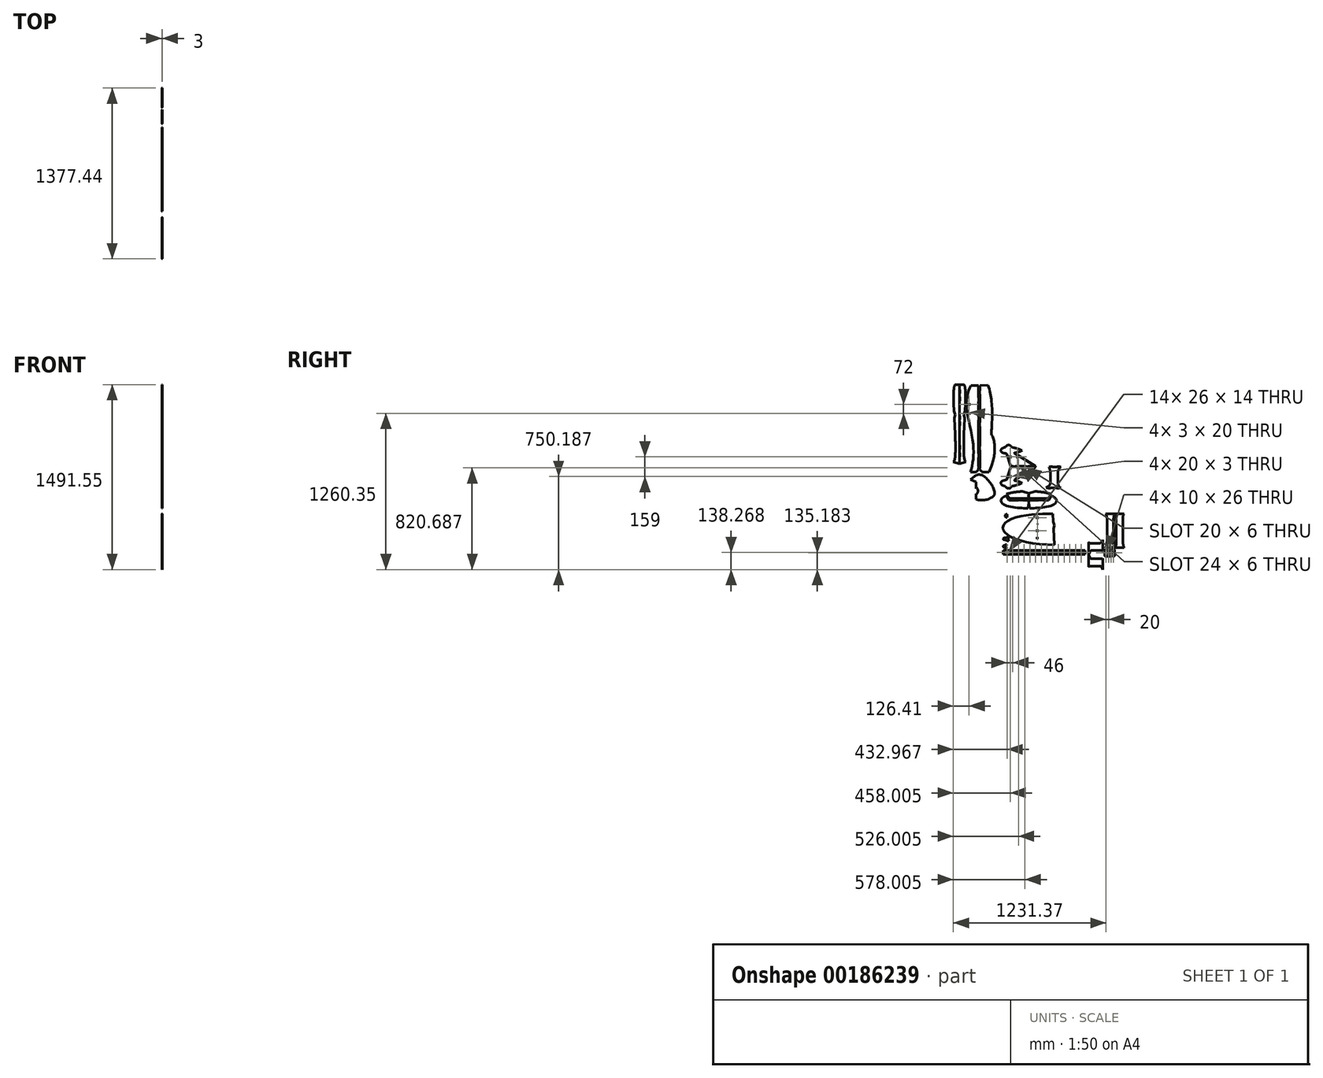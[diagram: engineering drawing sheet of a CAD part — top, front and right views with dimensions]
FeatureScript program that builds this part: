
annotation { "Feature Type Name" : "Feature", "Feature Type Description" : "" }
export const myFeature = defineFeature(function(context is Context, id is Id, definition is map)
    precondition{}
    {
        {
            var Q0;
            Q0=qCreatedBy(makeId("Right.planeOp"),FACE);
            var sketch = newSketch(context, id + "F0", { "sketchPlane" : qUnion([Q0])});
            skLineSegment(sketch, "E0", {"start": v(27.92, -28.88) * mm, "end": v(27.92, -378.88) * mm, "construction": true});
            skLineSegment(sketch, "E1", {"start": v(443.25, -23) * mm, "end": v(445.98, -85.39) * mm});
            skLineSegment(sketch, "E2", {"start": v(485.12, -6.25) * mm, "end": v(485.12, -297.85) * mm, "construction": true});
            skLineSegment(sketch, "E3", {"start": v(455, -114) * mm, "end": v(445.98, -85.39) * mm});
            skLineSegment(sketch, "E4", {"start": v(455, -114) * mm, "end": v(448.5, -143.29) * mm});
            skLineSegment(sketch, "E5.trimOffspring", {"start": v(448.5, -143.29) * mm, "end": v(454.12, -271.76) * mm});
            skFitSpline(sketch, "E6", {"points": [v(443.25, -23) * mm, v(273.48, -28) * mm, v(111.44, -63.42) * mm, v(51, -105.27) * mm, v(39.62, -138.6) * mm, v(65.24, -181.81) * mm, v(180.48, -236.77) * mm, v(454.12, -271.76) * mm], "startDerivative": vector(-965.41, -1.88) * mm, "endDerivative": vector(1440.75, 7.86) * mm});
            skLineSegment(sketch, "E7.bottom", {"start": v(316, -44) * mm, "end": v(319, -44) * mm});
            skLineSegment(sketch, "E7.top", {"start": v(316, -64) * mm, "end": v(319, -64) * mm});
            skLineSegment(sketch, "E7.left", {"start": v(316, -44) * mm, "end": v(316, -64) * mm});
            skLineSegment(sketch, "E7.right", {"start": v(319, -44) * mm, "end": v(319, -64) * mm});
            skLineSegment(sketch, "E8.bottom", {"start": v(316, -148) * mm, "end": v(319, -148) * mm});
            skLineSegment(sketch, "E8.top", {"start": v(316, -168) * mm, "end": v(319, -168) * mm});
            skLineSegment(sketch, "E8.left", {"start": v(316, -148) * mm, "end": v(316, -168) * mm});
            skLineSegment(sketch, "E8.right", {"start": v(319, -148) * mm, "end": v(319, -168) * mm});
            skLineSegment(sketch, "E9.bottom", {"start": v(316, -210) * mm, "end": v(319, -210) * mm});
            skLineSegment(sketch, "E9.top", {"start": v(316, -225) * mm, "end": v(319, -225) * mm});
            skLineSegment(sketch, "E9.left", {"start": v(316, -210) * mm, "end": v(316, -225) * mm});
            skLineSegment(sketch, "E9.right", {"start": v(319, -210) * mm, "end": v(319, -225) * mm});
            skCircle(sketch, "E10", {"center": v(320, -104.5) * mm, "radius": 1 * mm});
            skLineSegment(sketch, "E11", {"start": v(-356.55, 868.4) * mm, "end": v(-353.82, 806.01) * mm});
            skLineSegment(sketch, "E12", {"start": v(-309.8, 1019.4) * mm, "end": v(-309.8, 979.4) * mm});
            skLineSegment(sketch, "E13", {"start": v(-309.8, 380.9) * mm, "end": v(-359.91, 398.16) * mm});
            skLineSegment(sketch, "E14", {"start": v(-344.8, 777.4) * mm, "end": v(-353.82, 806.01) * mm});
            skLineSegment(sketch, "E15", {"start": v(-344.8, 777.4) * mm, "end": v(-351.3, 748.11) * mm});
            skLineSegment(sketch, "E16", {"start": v(-309.8, 1019.4) * mm, "end": v(-345.3, 1019.4) * mm});
            skLineSegment(sketch, "E17.trimOffspring", {"start": v(-351.3, 748.11) * mm, "end": v(-345.68, 619.64) * mm});
            skFitSpline(sketch, "E18", {"points": [v(-356.55, 868.4) * mm, v(-356.83, 968.97) * mm, v(-352.43, 1005.55) * mm, v(-349.11, 1014.93) * mm, v(-346.93, 1018.82) * mm, v(-345.3, 1019.4) * mm], "startDerivative": vector(-12.13, 345.27) * mm, "endDerivative": vector(43.94, 0.31) * mm});
            skFitSpline(sketch, "E19", {"points": [v(-345.68, 619.64) * mm, v(-342.97, 524.45) * mm, v(-346.35, 432.06) * mm, v(-353.3, 404.18) * mm, v(-359.91, 398.16) * mm], "startDerivative": vector(19, -544.1) * mm, "endDerivative": vector(-110.93, -29.86) * mm});
            skLineSegment(sketch, "E20", {"start": v(-309.8, 979.4) * mm, "end": v(-311.3, 979.4) * mm});
            skLineSegment(sketch, "E21", {"start": v(-311.3, 979.4) * mm, "end": v(-311.3, 949.4) * mm});
            skLineSegment(sketch, "E22", {"start": v(-311.3, 949.4) * mm, "end": v(-309.8, 949.4) * mm});
            skLineSegment(sketch, "E23", {"start": v(-309.8, 919.4) * mm, "end": v(-311.3, 919.4) * mm});
            skLineSegment(sketch, "E24", {"start": v(-311.3, 919.4) * mm, "end": v(-311.3, 889.4) * mm});
            skLineSegment(sketch, "E25", {"start": v(-311.3, 889.4) * mm, "end": v(-309.8, 889.4) * mm});
            skLineSegment(sketch, "E26", {"start": v(-309.8, 769.4) * mm, "end": v(-311.3, 769.4) * mm});
            skLineSegment(sketch, "E27", {"start": v(-311.3, 769.4) * mm, "end": v(-311.3, 739.4) * mm});
            skLineSegment(sketch, "E28", {"start": v(-311.3, 739.4) * mm, "end": v(-309.8, 739.4) * mm});
            skLineSegment(sketch, "E29", {"start": v(-309.8, 719.4) * mm, "end": v(-311.3, 719.4) * mm});
            skLineSegment(sketch, "E30", {"start": v(-311.3, 719.4) * mm, "end": v(-311.3, 689.4) * mm});
            skLineSegment(sketch, "E31", {"start": v(-311.3, 689.4) * mm, "end": v(-309.8, 689.4) * mm});
            skLineSegment(sketch, "E32", {"start": v(-309.8, 529.4) * mm, "end": v(-311.3, 529.4) * mm});
            skLineSegment(sketch, "E33", {"start": v(-311.3, 529.4) * mm, "end": v(-311.3, 499.4) * mm});
            skLineSegment(sketch, "E34", {"start": v(-311.3, 499.4) * mm, "end": v(-309.8, 499.4) * mm});
            skLineSegment(sketch, "E35", {"start": v(-309.8, 469.4) * mm, "end": v(-311.3, 469.4) * mm});
            skLineSegment(sketch, "E36", {"start": v(-311.3, 469.4) * mm, "end": v(-311.3, 439.4) * mm});
            skLineSegment(sketch, "E37", {"start": v(-311.3, 439.4) * mm, "end": v(-309.8, 439.4) * mm});
            skLineSegment(sketch, "E38.trimOffspring", {"start": v(-309.8, 949.4) * mm, "end": v(-309.8, 919.4) * mm});
            skLineSegment(sketch, "E39.trimOffspring", {"start": v(-309.8, 889.4) * mm, "end": v(-309.8, 769.4) * mm});
            skLineSegment(sketch, "E40.trimOffspring", {"start": v(-309.8, 739.4) * mm, "end": v(-309.8, 719.4) * mm});
            skLineSegment(sketch, "E41.trimOffspring", {"start": v(-309.8, 689.4) * mm, "end": v(-309.8, 529.4) * mm});
            skLineSegment(sketch, "E42.trimOffspring", {"start": v(-309.8, 499.4) * mm, "end": v(-309.8, 469.4) * mm});
            skLineSegment(sketch, "E43.trimOffspring", {"start": v(-309.8, 439.4) * mm, "end": v(-309.8, 380.9) * mm});
            skLineSegment(sketch, "E44", {"start": v(-144.2, 1013.2) * mm, "end": v(-144.2, 973.2) * mm});
            skLineSegment(sketch, "E45", {"start": v(-144.2, 334.7) * mm, "end": v(-124.7, 314.56) * mm});
            skLineSegment(sketch, "E46", {"start": v(-124.7, 314.56) * mm, "end": v(-72.7, 314.56) * mm});
            skLineSegment(sketch, "E47", {"start": v(-144.2, 973.2) * mm, "end": v(-147.2, 973.2) * mm});
            skLineSegment(sketch, "E48", {"start": v(-147.2, 973.2) * mm, "end": v(-147.2, 943.2) * mm});
            skLineSegment(sketch, "E49", {"start": v(-147.2, 943.2) * mm, "end": v(-144.2, 943.2) * mm});
            skLineSegment(sketch, "E50", {"start": v(-144.2, 713.2) * mm, "end": v(-147.2, 713.2) * mm});
            skLineSegment(sketch, "E51", {"start": v(-147.2, 713.2) * mm, "end": v(-147.2, 683.2) * mm});
            skLineSegment(sketch, "E52", {"start": v(-147.2, 683.2) * mm, "end": v(-144.2, 683.2) * mm});
            skLineSegment(sketch, "E53", {"start": v(-144.2, 523.2) * mm, "end": v(-147.2, 523.2) * mm});
            skLineSegment(sketch, "E54", {"start": v(-147.2, 523.2) * mm, "end": v(-147.2, 493.2) * mm});
            skLineSegment(sketch, "E55", {"start": v(-147.2, 493.2) * mm, "end": v(-144.2, 493.2) * mm});
            skLineSegment(sketch, "E56", {"start": v(-144.2, 344.7) * mm, "end": v(-147.2, 344.7) * mm});
            skLineSegment(sketch, "E57", {"start": v(-147.2, 344.7) * mm, "end": v(-147.2, 334.7) * mm});
            skLineSegment(sketch, "E58", {"start": v(-147.2, 334.7) * mm, "end": v(-144.2, 334.7) * mm});
            skLineSegment(sketch, "E59.trimOffspring", {"start": v(-144.2, 493.2) * mm, "end": v(-144.2, 344.7) * mm});
            skLineSegment(sketch, "E60.trimOffspring", {"start": v(-144.2, 683.2) * mm, "end": v(-144.2, 523.2) * mm});
            skLineSegment(sketch, "E61.trimOffspring", {"start": v(-144.2, 943.2) * mm, "end": v(-144.2, 713.2) * mm});
            skLineSegment(sketch, "E62", {"start": v(-144.2, 1013.2) * mm, "end": v(-82.22, 1014.82) * mm});
            skFitSpline(sketch, "E63", {"points": [v(-82.22, 1014.82) * mm, v(-52.5, 891.86) * mm, v(-47.86, 740.86) * mm, v(-54.44, 620.7) * mm], "startDerivative": vector(163.45, -369.94) * mm, "endDerivative": vector(-24, -362.98) * mm});
            skLineSegment(sketch, "E64", {"start": v(-157, 1013.2) * mm, "end": v(-157, 913.2) * mm});
            skLineSegment(sketch, "E65", {"start": v(-157, 334.7) * mm, "end": v(-177, 314.56) * mm});
            skLineSegment(sketch, "E66", {"start": v(-177, 314.56) * mm, "end": v(-222, 314.56) * mm});
            skLineSegment(sketch, "E67", {"start": v(-157, 1013.2) * mm, "end": v(-218.98, 1011.58) * mm});
            skLineSegment(sketch, "E68", {"start": v(-157, 913.2) * mm, "end": v(-154, 913.2) * mm});
            skLineSegment(sketch, "E69", {"start": v(-154, 913.2) * mm, "end": v(-154, 883.2) * mm});
            skLineSegment(sketch, "E70", {"start": v(-154, 883.2) * mm, "end": v(-157, 883.2) * mm});
            skLineSegment(sketch, "E71", {"start": v(-157, 763.2) * mm, "end": v(-154, 763.2) * mm});
            skLineSegment(sketch, "E72", {"start": v(-154, 763.2) * mm, "end": v(-154, 733.2) * mm});
            skLineSegment(sketch, "E73", {"start": v(-154, 733.2) * mm, "end": v(-157, 733.2) * mm});
            skLineSegment(sketch, "E74", {"start": v(-157, 463.2) * mm, "end": v(-154, 463.2) * mm});
            skLineSegment(sketch, "E75", {"start": v(-154, 463.2) * mm, "end": v(-154, 433.2) * mm});
            skLineSegment(sketch, "E76", {"start": v(-154, 433.2) * mm, "end": v(-157, 433.2) * mm});
            skLineSegment(sketch, "E77", {"start": v(-157, 359.7) * mm, "end": v(-154, 359.7) * mm});
            skLineSegment(sketch, "E78", {"start": v(-154, 359.7) * mm, "end": v(-154, 349.7) * mm});
            skLineSegment(sketch, "E79", {"start": v(-154, 349.7) * mm, "end": v(-157, 349.7) * mm});
            skLineSegment(sketch, "E80.trimOffspring", {"start": v(-157, 349.7) * mm, "end": v(-157, 334.7) * mm});
            skLineSegment(sketch, "E81.trimOffspring", {"start": v(-157, 433.2) * mm, "end": v(-157, 359.7) * mm});
            skLineSegment(sketch, "E82.trimOffspring", {"start": v(-157, 733.2) * mm, "end": v(-157, 463.2) * mm});
            skLineSegment(sketch, "E83.trimOffspring", {"start": v(-157, 883.2) * mm, "end": v(-157, 763.2) * mm});
            skFitSpline(sketch, "E84", {"points": [v(-222, 314.56) * mm, v(-200.27, 420.75) * mm, v(-204.03, 569.28) * mm, v(-247.79, 793.5) * mm, v(-249.4, 929.59) * mm, v(-218.98, 1011.58) * mm], "startDerivative": vector(155.72, 450.4) * mm, "endDerivative": vector(203.74, 370.62) * mm});
            skLineSegment(sketch, "E85", {"start": v(-176.43, 234.38) * mm, "end": v(-176.43, 182.38) * mm});
            skLineSegment(sketch, "E86", {"start": v(-176.43, 139.88) * mm, "end": v(-176.43, 94.88) * mm});
            skArc(sketch, "E87", {"start": v(-119.34, 284.4) * mm, "mid": v(-152.52, 294.07) * mm, "end": v(-185.06, 282.42) * mm});
            skArc(sketch, "E88", {"start": v(-40.5, 117.7) * mm, "mid": v(-28.29, 134.7) * mm, "end": v(-27.63, 155.64) * mm});
            skArc(sketch, "E89", {"start": v(-176.43, 94.88) * mm, "mid": v(-105.63, 89.44) * mm, "end": v(-40.5, 117.7) * mm});
            skArc(sketch, "E90", {"start": v(-27.63, 155.64) * mm, "mid": v(-61.96, 228.23) * mm, "end": v(-119.34, 284.4) * mm});
            skLineSegment(sketch, "E91", {"start": v(-222.68, 253.38) * mm, "end": v(-185.06, 282.42) * mm});
            skPoint(sketch, "E92", {"position": v(-53.7, 360.81) * mm});
            skLineSegment(sketch, "E93", {"start": v(-72.7, 314.56) * mm, "end": v(-53.7, 360.81) * mm});
            skFitSpline(sketch, "E94", {"points": [v(-53.7, 360.81) * mm, v(-30.19, 450.47) * mm, v(-30.24, 553.44) * mm, v(-54.44, 620.7) * mm], "startDerivative": vector(84.05, 239.81) * mm, "endDerivative": vector(-123.94, 199.65) * mm});
            skLineSegment(sketch, "E95", {"start": v(-176.43, 234.38) * mm, "end": v(-222.68, 253.38) * mm});
            skLineSegment(sketch, "E96", {"start": v(248.03, 141.56) * mm, "end": v(248.03, 126.56) * mm});
            skLineSegment(sketch, "E97", {"start": v(248.03, 111.56) * mm, "end": v(246.53, 111.56) * mm});
            skLineSegment(sketch, "E98", {"start": v(246.53, 111.56) * mm, "end": v(246.53, 101.56) * mm});
            skLineSegment(sketch, "E99", {"start": v(246.53, 101.56) * mm, "end": v(88.53, 101.56) * mm});
            skLineSegment(sketch, "E100", {"start": v(88.53, 101.56) * mm, "end": v(68.03, 137.06) * mm});
            skLineSegment(sketch, "E101", {"start": v(248.03, 141.56) * mm, "end": v(197.92, 158.81) * mm});
            skLineSegment(sketch, "E102", {"start": v(248.03, 116.56) * mm, "end": v(246.53, 116.56) * mm});
            skLineSegment(sketch, "E103", {"start": v(246.53, 116.56) * mm, "end": v(246.53, 126.56) * mm});
            skLineSegment(sketch, "E104", {"start": v(246.53, 126.56) * mm, "end": v(248.03, 126.56) * mm});
            skLineSegment(sketch, "E105.trimOffspring", {"start": v(248.03, 116.56) * mm, "end": v(248.03, 111.56) * mm});
            skFitSpline(sketch, "E106", {"points": [v(68.03, 137.06) * mm, v(127.3, 151) * mm, v(197.92, 158.81) * mm], "startDerivative": vector(116.05, 38.24) * mm, "endDerivative": vector(126.97, 8.86) * mm});
            skLineSegment(sketch, "E107", {"start": v(68.03, 122.99) * mm, "end": v(88.53, 87.48) * mm});
            skLineSegment(sketch, "E108", {"start": v(88.53, 87.48) * mm, "end": v(248.03, 87.48) * mm});
            skLineSegment(sketch, "E109", {"start": v(248.03, 87.48) * mm, "end": v(248.03, 55.48) * mm});
            skLineSegment(sketch, "E110", {"start": v(248.03, 55.48) * mm, "end": v(244.03, 55.48) * mm});
            skLineSegment(sketch, "E111", {"start": v(244.03, 55.48) * mm, "end": v(241.73, 22.56) * mm});
            skFitSpline(sketch, "E112", {"points": [v(68.03, 122.99) * mm, v(36.37, 107.72) * mm, v(23.55, 87.23) * mm, v(38.07, 58.37) * mm, v(125.76, 29.82) * mm, v(241.73, 22.56) * mm], "startDerivative": vector(-166.1, -58.4) * mm, "endDerivative": vector(399.12, -7.54) * mm});
            skLineSegment(sketch, "E113", {"start": v(101.1, 354.54) * mm, "end": v(120.1, 354.54) * mm});
            skLineSegment(sketch, "E114", {"start": v(120.1, 354.54) * mm, "end": v(120.1, 357.54) * mm});
            skLineSegment(sketch, "E115", {"start": v(120.1, 357.54) * mm, "end": v(140.1, 357.54) * mm});
            skLineSegment(sketch, "E116", {"start": v(140.1, 357.54) * mm, "end": v(140.1, 354.54) * mm});
            skLineSegment(sketch, "E117", {"start": v(140.1, 354.54) * mm, "end": v(224.1, 354.54) * mm});
            skLineSegment(sketch, "E118", {"start": v(224.1, 354.54) * mm, "end": v(224.1, 357.54) * mm});
            skLineSegment(sketch, "E119", {"start": v(224.1, 357.54) * mm, "end": v(244.1, 357.54) * mm});
            skLineSegment(sketch, "E120", {"start": v(244.1, 357.54) * mm, "end": v(244.1, 354.54) * mm});
            skLineSegment(sketch, "E121", {"start": v(244.1, 354.54) * mm, "end": v(286.1, 354.54) * mm});
            skLineSegment(sketch, "E122", {"start": v(286.1, 354.54) * mm, "end": v(286.1, 357.54) * mm});
            skLineSegment(sketch, "E123", {"start": v(286.1, 357.54) * mm, "end": v(301.1, 357.54) * mm});
            skLineSegment(sketch, "E124", {"start": v(301.1, 357.54) * mm, "end": v(301.1, 354.54) * mm});
            skLineSegment(sketch, "E125", {"start": v(301.1, 354.54) * mm, "end": v(128.72, 246.8) * mm});
            skLineSegment(sketch, "E126", {"start": v(101.1, 354.54) * mm, "end": v(69.08, 251.02) * mm});
            skFitSpline(sketch, "E127", {"points": [v(69.08, 251.02) * mm, v(30.4, 239.54) * mm, v(23.23, 226.4) * mm, v(31.82, 210.74) * mm, v(60.87, 200.12) * mm], "startDerivative": vector(-185.57, -20.9) * mm, "endDerivative": vector(122.55, -13.98) * mm});
            skFitSpline(sketch, "E128", {"points": [v(128.72, 246.8) * mm, v(164.15, 239.14) * mm, v(193.63, 226.66) * mm], "startDerivative": vector(69.66, -10.84) * mm, "endDerivative": vector(67.95, -41.44) * mm});
            skFitSpline(sketch, "E129", {"points": [v(193.63, 226.66) * mm, v(152.17, 210.06) * mm, v(110.29, 200.98) * mm], "startDerivative": vector(-63.37, -40.2) * mm, "endDerivative": vector(-87.44, -10.73) * mm});
            skArc(sketch, "E130", {"start": v(60.87, 200.12) * mm, "mid": v(85.89, 182.63) * mm, "end": v(110.29, 200.98) * mm});
            skLineSegment(sketch, "E131.bottom", {"start": v(-235, 870.2) * mm, "end": v(-232, 870.2) * mm});
            skLineSegment(sketch, "E131.top", {"start": v(-235, 850.2) * mm, "end": v(-232, 850.2) * mm});
            skLineSegment(sketch, "E131.left", {"start": v(-235, 870.2) * mm, "end": v(-235, 850.2) * mm});
            skLineSegment(sketch, "E131.right", {"start": v(-232, 870.2) * mm, "end": v(-232, 850.2) * mm});
            skLineSegment(sketch, "E132.bottom", {"start": v(-235, 798.2) * mm, "end": v(-232, 798.2) * mm});
            skLineSegment(sketch, "E132.top", {"start": v(-235, 778.2) * mm, "end": v(-232, 778.2) * mm});
            skLineSegment(sketch, "E132.left", {"start": v(-235, 798.2) * mm, "end": v(-235, 778.2) * mm});
            skLineSegment(sketch, "E132.right", {"start": v(-232, 798.2) * mm, "end": v(-232, 778.2) * mm});
            skLineSegment(sketch, "E133.bottom", {"start": v(88.1, 279.54) * mm, "end": v(108.1, 279.54) * mm});
            skLineSegment(sketch, "E133.top", {"start": v(88.1, 276.54) * mm, "end": v(108.1, 276.54) * mm});
            skLineSegment(sketch, "E133.left", {"start": v(88.1, 279.54) * mm, "end": v(88.1, 276.54) * mm});
            skLineSegment(sketch, "E133.right", {"start": v(108.1, 279.54) * mm, "end": v(108.1, 276.54) * mm});
            skLineSegment(sketch, "E134.bottom", {"start": v(146.1, 279.54) * mm, "end": v(166.1, 279.54) * mm});
            skLineSegment(sketch, "E134.top", {"start": v(146.1, 276.54) * mm, "end": v(166.1, 276.54) * mm});
            skLineSegment(sketch, "E134.left", {"start": v(146.1, 279.54) * mm, "end": v(146.1, 276.54) * mm});
            skLineSegment(sketch, "E134.right", {"start": v(166.1, 279.54) * mm, "end": v(166.1, 276.54) * mm});
            skLineSegment(sketch, "E135", {"start": v(409, 355.87) * mm, "end": v(420, 355.87) * mm});
            skLineSegment(sketch, "E136", {"start": v(420, 355.87) * mm, "end": v(420, 358.87) * mm});
            skLineSegment(sketch, "E137", {"start": v(420, 358.87) * mm, "end": v(440, 358.87) * mm});
            skLineSegment(sketch, "E138", {"start": v(440, 358.87) * mm, "end": v(440, 355.87) * mm});
            skLineSegment(sketch, "E139", {"start": v(440, 355.87) * mm, "end": v(478, 355.87) * mm});
            skLineSegment(sketch, "E140", {"start": v(478, 355.87) * mm, "end": v(478, 358.87) * mm});
            skLineSegment(sketch, "E141", {"start": v(478, 358.87) * mm, "end": v(498, 358.87) * mm});
            skLineSegment(sketch, "E142", {"start": v(498, 358.87) * mm, "end": v(498, 355.87) * mm});
            skLineSegment(sketch, "E143", {"start": v(498, 355.87) * mm, "end": v(508, 355.87) * mm});
            skLineSegment(sketch, "E144", {"start": v(409, 355.87) * mm, "end": v(415.72, 341.95) * mm});
            skLineSegment(sketch, "E145", {"start": v(423.45, 308.09) * mm, "end": v(423.45, 233.94) * mm});
            skLineSegment(sketch, "E146", {"start": v(388, 186.37) * mm, "end": v(404.2, 197.45) * mm});
            skLineSegment(sketch, "E147", {"start": v(388, 186.37) * mm, "end": v(403, 186.37) * mm});
            skLineSegment(sketch, "E148", {"start": v(403, 186.37) * mm, "end": v(403, 184.87) * mm});
            skLineSegment(sketch, "E149", {"start": v(403, 184.87) * mm, "end": v(423, 184.87) * mm});
            skLineSegment(sketch, "E150", {"start": v(423, 184.87) * mm, "end": v(423, 186.37) * mm});
            skLineSegment(sketch, "E151", {"start": v(423, 186.37) * mm, "end": v(475, 186.37) * mm});
            skLineSegment(sketch, "E152", {"start": v(475, 186.37) * mm, "end": v(475, 184.87) * mm});
            skLineSegment(sketch, "E153", {"start": v(475, 184.87) * mm, "end": v(495, 184.87) * mm});
            skLineSegment(sketch, "E154", {"start": v(495, 184.87) * mm, "end": v(495, 186.37) * mm});
            skLineSegment(sketch, "E155", {"start": v(495, 186.37) * mm, "end": v(507, 186.37) * mm});
            skLineSegment(sketch, "E156", {"start": v(484.82, 221.62) * mm, "end": v(484.82, 318.58) * mm});
            skArc(sketch, "E157", {"start": v(508, 355.87) * mm, "mid": v(491.09, 340.54) * mm, "end": v(484.82, 318.58) * mm});
            skArc(sketch, "E158", {"start": v(484.82, 221.62) * mm, "mid": v(490.83, 200.8) * mm, "end": v(507, 186.37) * mm});
            skArc(sketch, "E159", {"start": v(423.45, 308.09) * mm, "mid": v(421.5, 325.45) * mm, "end": v(415.72, 341.95) * mm});
            skArc(sketch, "E160", {"start": v(404.2, 197.45) * mm, "mid": v(418.35, 213.31) * mm, "end": v(423.45, 233.94) * mm});
            skLineSegment(sketch, "E161", {"start": v(729.86, -351.15) * mm, "end": v(729.86, -252.15) * mm});
            skLineSegment(sketch, "E162", {"start": v(745.23, -259.1) * mm, "end": v(820.62, -259.1) * mm});
            skLineSegment(sketch, "E163", {"start": v(844.86, -230.15) * mm, "end": v(844.86, -320.15) * mm});
            skLineSegment(sketch, "E164", {"start": v(759.7, -316.87) * mm, "end": v(832.36, -316.87) * mm});
            skLineSegment(sketch, "E165", {"start": v(729.86, -351.15) * mm, "end": v(739.35, -330.04) * mm});
            skLineSegment(sketch, "E166", {"start": v(844.86, -230.15) * mm, "end": v(835.95, -249.32) * mm});
            skArc(sketch, "E167", {"start": v(759.7, -316.87) * mm, "mid": v(747.58, -320.45) * mm, "end": v(739.35, -330.04) * mm});
            skArc(sketch, "E168", {"start": v(844.86, -320.15) * mm, "mid": v(838.82, -317.7) * mm, "end": v(832.36, -316.87) * mm});
            skArc(sketch, "E169", {"start": v(729.86, -252.15) * mm, "mid": v(736.8, -257.29) * mm, "end": v(745.23, -259.1) * mm});
            skArc(sketch, "E170", {"start": v(820.62, -259.1) * mm, "mid": v(829.72, -256.45) * mm, "end": v(835.95, -249.32) * mm});
            skLineSegment(sketch, "E171", {"start": v(867.53, -21.62) * mm, "end": v(942.53, -21.62) * mm});
            skLineSegment(sketch, "E172", {"start": v(878.96, -57.62) * mm, "end": v(878.96, -235.17) * mm});
            skLineSegment(sketch, "E173", {"start": v(867.53, -296.62) * mm, "end": v(942.53, -296.62) * mm});
            skLineSegment(sketch, "E174", {"start": v(932.35, -266.1) * mm, "end": v(932.35, -61.06) * mm});
            skArc(sketch, "E175", {"start": v(878.96, -57.62) * mm, "mid": v(876.04, -38.74) * mm, "end": v(867.53, -21.62) * mm});
            skArc(sketch, "E176", {"start": v(867.53, -296.62) * mm, "mid": v(876.08, -266.42) * mm, "end": v(878.96, -235.17) * mm});
            skArc(sketch, "E177", {"start": v(942.53, -21.62) * mm, "mid": v(934.94, -40.7) * mm, "end": v(932.35, -61.06) * mm});
            skArc(sketch, "E178", {"start": v(932.35, -266.1) * mm, "mid": v(934.97, -282.19) * mm, "end": v(942.53, -296.62) * mm});
            skLineSegment(sketch, "E179.bottom", {"start": v(42.06, -317.88) * mm, "end": v(702.06, -317.88) * mm});
            skLineSegment(sketch, "E179.top", {"start": v(42.06, -349.88) * mm, "end": v(702.06, -349.88) * mm});
            skLineSegment(sketch, "E179.left", {"start": v(42.06, -317.88) * mm, "end": v(42.06, -349.88) * mm});
            skLineSegment(sketch, "E179.right", {"start": v(702.06, -317.88) * mm, "end": v(702.06, -349.88) * mm});
            skLineSegment(sketch, "E180", {"start": v(60.06, -333.88) * mm, "end": v(73.06, -326.88) * mm});
            skLineSegment(sketch, "E181", {"start": v(73.06, -326.88) * mm, "end": v(86.06, -333.88) * mm});
            skLineSegment(sketch, "E182", {"start": v(86.06, -333.88) * mm, "end": v(60.06, -333.88) * mm, "construction": true});
            skLineSegment(sketch, "E183", {"start": v(73.06, -333.88) * mm, "end": v(73.06, -326.88) * mm, "construction": true});
            skLineSegment(sketch, "E184.MirrorCS", {"start": v(60.06, -333.88) * mm, "end": v(73.06, -340.88) * mm});
            skLineSegment(sketch, "E185.MirrorCS", {"start": v(73.06, -340.88) * mm, "end": v(86.06, -333.88) * mm});
            skLineSegment(sketch, "E186.1.0.0", {"start": v(119.06, -326.88) * mm, "end": v(132.06, -333.88) * mm});
            skLineSegment(sketch, "E186.1.0.1", {"start": v(106.06, -333.88) * mm, "end": v(119.06, -326.88) * mm});
            skLineSegment(sketch, "E186.1.0.2", {"start": v(106.06, -333.88) * mm, "end": v(119.06, -340.88) * mm});
            skLineSegment(sketch, "E186.1.0.3", {"start": v(119.06, -340.88) * mm, "end": v(132.06, -333.88) * mm});
            skLineSegment(sketch, "E186.2.0.0", {"start": v(165.06, -326.88) * mm, "end": v(178.06, -333.88) * mm});
            skLineSegment(sketch, "E186.2.0.1", {"start": v(152.06, -333.88) * mm, "end": v(165.06, -326.88) * mm});
            skLineSegment(sketch, "E186.2.0.2", {"start": v(152.06, -333.88) * mm, "end": v(165.06, -340.88) * mm});
            skLineSegment(sketch, "E186.2.0.3", {"start": v(165.06, -340.88) * mm, "end": v(178.06, -333.88) * mm});
            skLineSegment(sketch, "E186.direction1", {"start": v(73.06, -326.88) * mm, "end": v(119.06, -326.88) * mm, "construction": true});
            skLineSegment(sketch, "E187.0.3.0", {"start": v(211.06, -326.88) * mm, "end": v(224.06, -333.88) * mm});
            skLineSegment(sketch, "E187.3.3.0", {"start": v(198.06, -333.88) * mm, "end": v(211.06, -326.88) * mm});
            skLineSegment(sketch, "E187.6.3.0", {"start": v(198.06, -333.88) * mm, "end": v(211.06, -340.88) * mm});
            skLineSegment(sketch, "E187.9.3.0", {"start": v(211.06, -340.88) * mm, "end": v(224.06, -333.88) * mm});
            skLineSegment(sketch, "E187.0.4.0", {"start": v(257.06, -326.88) * mm, "end": v(270.06, -333.88) * mm});
            skLineSegment(sketch, "E187.3.4.0", {"start": v(244.06, -333.88) * mm, "end": v(257.06, -326.88) * mm});
            skLineSegment(sketch, "E187.6.4.0", {"start": v(244.06, -333.88) * mm, "end": v(257.06, -340.88) * mm});
            skLineSegment(sketch, "E187.9.4.0", {"start": v(257.06, -340.88) * mm, "end": v(270.06, -333.88) * mm});
            skLineSegment(sketch, "E187.0.5.0", {"start": v(303.06, -326.88) * mm, "end": v(316.06, -333.88) * mm});
            skLineSegment(sketch, "E187.3.5.0", {"start": v(290.06, -333.88) * mm, "end": v(303.06, -326.88) * mm});
            skLineSegment(sketch, "E187.6.5.0", {"start": v(290.06, -333.88) * mm, "end": v(303.06, -340.88) * mm});
            skLineSegment(sketch, "E187.9.5.0", {"start": v(303.06, -340.88) * mm, "end": v(316.06, -333.88) * mm});
            skLineSegment(sketch, "E187.0.6.0", {"start": v(349.06, -326.88) * mm, "end": v(362.06, -333.88) * mm});
            skLineSegment(sketch, "E187.3.6.0", {"start": v(336.06, -333.88) * mm, "end": v(349.06, -326.88) * mm});
            skLineSegment(sketch, "E187.6.6.0", {"start": v(336.06, -333.88) * mm, "end": v(349.06, -340.88) * mm});
            skLineSegment(sketch, "E187.9.6.0", {"start": v(349.06, -340.88) * mm, "end": v(362.06, -333.88) * mm});
            skLineSegment(sketch, "E187.0.7.0", {"start": v(395.06, -326.88) * mm, "end": v(408.06, -333.88) * mm});
            skLineSegment(sketch, "E187.3.7.0", {"start": v(382.06, -333.88) * mm, "end": v(395.06, -326.88) * mm});
            skLineSegment(sketch, "E187.6.7.0", {"start": v(382.06, -333.88) * mm, "end": v(395.06, -340.88) * mm});
            skLineSegment(sketch, "E187.9.7.0", {"start": v(395.06, -340.88) * mm, "end": v(408.06, -333.88) * mm});
            skLineSegment(sketch, "E187.0.8.0", {"start": v(441.06, -326.88) * mm, "end": v(454.06, -333.88) * mm});
            skLineSegment(sketch, "E187.3.8.0", {"start": v(428.06, -333.88) * mm, "end": v(441.06, -326.88) * mm});
            skLineSegment(sketch, "E187.6.8.0", {"start": v(428.06, -333.88) * mm, "end": v(441.06, -340.88) * mm});
            skLineSegment(sketch, "E187.9.8.0", {"start": v(441.06, -340.88) * mm, "end": v(454.06, -333.88) * mm});
            skLineSegment(sketch, "E187.0.9.0", {"start": v(487.06, -326.88) * mm, "end": v(500.06, -333.88) * mm});
            skLineSegment(sketch, "E187.3.9.0", {"start": v(474.06, -333.88) * mm, "end": v(487.06, -326.88) * mm});
            skLineSegment(sketch, "E187.6.9.0", {"start": v(474.06, -333.88) * mm, "end": v(487.06, -340.88) * mm});
            skLineSegment(sketch, "E187.9.9.0", {"start": v(487.06, -340.88) * mm, "end": v(500.06, -333.88) * mm});
            skLineSegment(sketch, "E187.0.10.0", {"start": v(533.06, -326.88) * mm, "end": v(546.06, -333.88) * mm});
            skLineSegment(sketch, "E187.3.10.0", {"start": v(520.06, -333.88) * mm, "end": v(533.06, -326.88) * mm});
            skLineSegment(sketch, "E187.6.10.0", {"start": v(520.06, -333.88) * mm, "end": v(533.06, -340.88) * mm});
            skLineSegment(sketch, "E187.9.10.0", {"start": v(533.06, -340.88) * mm, "end": v(546.06, -333.88) * mm});
            skLineSegment(sketch, "E187.0.11.0", {"start": v(579.06, -326.88) * mm, "end": v(592.06, -333.88) * mm});
            skLineSegment(sketch, "E187.3.11.0", {"start": v(566.06, -333.88) * mm, "end": v(579.06, -326.88) * mm});
            skLineSegment(sketch, "E187.6.11.0", {"start": v(566.06, -333.88) * mm, "end": v(579.06, -340.88) * mm});
            skLineSegment(sketch, "E187.9.11.0", {"start": v(579.06, -340.88) * mm, "end": v(592.06, -333.88) * mm});
            skLineSegment(sketch, "E187.0.12.0", {"start": v(625.06, -326.88) * mm, "end": v(638.06, -333.88) * mm});
            skLineSegment(sketch, "E187.3.12.0", {"start": v(612.06, -333.88) * mm, "end": v(625.06, -326.88) * mm});
            skLineSegment(sketch, "E187.6.12.0", {"start": v(612.06, -333.88) * mm, "end": v(625.06, -340.88) * mm});
            skLineSegment(sketch, "E187.9.12.0", {"start": v(625.06, -340.88) * mm, "end": v(638.06, -333.88) * mm});
            skLineSegment(sketch, "E187.0.13.0", {"start": v(671.06, -326.88) * mm, "end": v(684.06, -333.88) * mm});
            skLineSegment(sketch, "E187.3.13.0", {"start": v(658.06, -333.88) * mm, "end": v(671.06, -326.88) * mm});
            skLineSegment(sketch, "E187.6.13.0", {"start": v(658.06, -333.88) * mm, "end": v(671.06, -340.88) * mm});
            skLineSegment(sketch, "E187.9.13.0", {"start": v(671.06, -340.88) * mm, "end": v(684.06, -333.88) * mm});
            skLineSegment(sketch, "E188.bottom", {"start": v(866.46, -309.97) * mm, "end": v(879.8, -309.97) * mm});
            skLineSegment(sketch, "E188.top", {"start": v(866.46, -363.97) * mm, "end": v(879.8, -363.97) * mm});
            skLineSegment(sketch, "E188.left", {"start": v(861.46, -314.97) * mm, "end": v(861.46, -358.97) * mm});
            skLineSegment(sketch, "E188.right", {"start": v(941.46, -314.97) * mm, "end": v(941.46, -358.97) * mm});
            skLineSegment(sketch, "E189", {"start": v(899.8, -309.97) * mm, "end": v(901.46, -313.97) * mm});
            skLineSegment(sketch, "E190", {"start": v(901.46, -313.97) * mm, "end": v(903.12, -309.97) * mm});
            skLineSegment(sketch, "E191", {"start": v(901.46, -313.97) * mm, "end": v(901.46, -309.97) * mm, "construction": true});
            skLineSegment(sketch, "E192.trimOffspring", {"start": v(901.46, -309.97) * mm, "end": v(919.8, -309.97) * mm});
            skLineSegment(sketch, "E193.1.0.0", {"start": v(919.8, -309.97) * mm, "end": v(921.46, -313.97) * mm});
            skLineSegment(sketch, "E193.1.0.1", {"start": v(921.46, -313.97) * mm, "end": v(923.12, -309.97) * mm});
            skLineSegment(sketch, "E193.direction1", {"start": v(901.46, -313.97) * mm, "end": v(921.46, -313.97) * mm, "construction": true});
            skLineSegment(sketch, "E194.1.0.0", {"start": v(879.8, -309.97) * mm, "end": v(881.46, -313.97) * mm});
            skLineSegment(sketch, "E194.1.0.1", {"start": v(881.46, -313.97) * mm, "end": v(883.12, -309.97) * mm});
            skLineSegment(sketch, "E194.direction1", {"start": v(901.46, -313.97) * mm, "end": v(881.46, -313.97) * mm, "construction": true});
            skLineSegment(sketch, "E195.trimOffspring", {"start": v(883.12, -309.97) * mm, "end": v(899.8, -309.97) * mm});
            skLineSegment(sketch, "E196.trimOffspring", {"start": v(923.12, -309.97) * mm, "end": v(936.46, -309.97) * mm});
            skLineSegment(sketch, "E197", {"start": v(861.46, -336.97) * mm, "end": v(941.46, -336.97) * mm, "construction": true});
            skLineSegment(sketch, "E198", {"start": v(866.46, -336.97) * mm, "end": v(871.46, -323.97) * mm});
            skLineSegment(sketch, "E199", {"start": v(871.46, -323.97) * mm, "end": v(876.46, -336.97) * mm});
            skLineSegment(sketch, "E200", {"start": v(871.46, -323.97) * mm, "end": v(871.46, -336.97) * mm, "construction": true});
            skLineSegment(sketch, "E201.MirrorCS", {"start": v(866.46, -336.97) * mm, "end": v(871.46, -349.97) * mm});
            skLineSegment(sketch, "E202.MirrorCS", {"start": v(871.46, -349.97) * mm, "end": v(876.46, -336.97) * mm});
            skLineSegment(sketch, "E203.MirrorCS", {"start": v(879.8, -363.97) * mm, "end": v(881.46, -359.97) * mm});
            skLineSegment(sketch, "E204.MirrorCS", {"start": v(881.46, -359.97) * mm, "end": v(883.12, -363.97) * mm});
            skLineSegment(sketch, "E205.MirrorCS", {"start": v(899.8, -363.97) * mm, "end": v(901.46, -359.97) * mm});
            skLineSegment(sketch, "E206.MirrorCS", {"start": v(901.46, -359.97) * mm, "end": v(903.12, -363.97) * mm});
            skLineSegment(sketch, "E207.MirrorCS", {"start": v(921.46, -359.97) * mm, "end": v(923.12, -363.97) * mm});
            skLineSegment(sketch, "E208.MirrorCS", {"start": v(919.8, -363.97) * mm, "end": v(921.46, -359.97) * mm});
            skLineSegment(sketch, "E209.1.0.0", {"start": v(886.46, -336.97) * mm, "end": v(891.46, -323.97) * mm});
            skLineSegment(sketch, "E209.1.0.1", {"start": v(891.46, -323.97) * mm, "end": v(896.46, -336.97) * mm});
            skLineSegment(sketch, "E209.1.0.2", {"start": v(891.46, -349.97) * mm, "end": v(896.46, -336.97) * mm});
            skLineSegment(sketch, "E209.1.0.3", {"start": v(886.46, -336.97) * mm, "end": v(891.46, -349.97) * mm});
            skLineSegment(sketch, "E209.2.0.0", {"start": v(906.46, -336.97) * mm, "end": v(911.46, -323.97) * mm});
            skLineSegment(sketch, "E209.2.0.1", {"start": v(911.46, -323.97) * mm, "end": v(916.46, -336.97) * mm});
            skLineSegment(sketch, "E209.2.0.2", {"start": v(911.46, -349.97) * mm, "end": v(916.46, -336.97) * mm});
            skLineSegment(sketch, "E209.2.0.3", {"start": v(906.46, -336.97) * mm, "end": v(911.46, -349.97) * mm});
            skLineSegment(sketch, "E209.direction1", {"start": v(866.46, -336.97) * mm, "end": v(886.46, -336.97) * mm, "construction": true});
            skLineSegment(sketch, "E210.0.3.0", {"start": v(926.46, -336.97) * mm, "end": v(931.46, -323.97) * mm});
            skLineSegment(sketch, "E210.3.3.0", {"start": v(931.46, -323.97) * mm, "end": v(936.46, -336.97) * mm});
            skLineSegment(sketch, "E210.6.3.0", {"start": v(931.46, -349.97) * mm, "end": v(936.46, -336.97) * mm});
            skLineSegment(sketch, "E210.9.3.0", {"start": v(926.46, -336.97) * mm, "end": v(931.46, -349.97) * mm});
            skLineSegment(sketch, "E211.trimOffspring", {"start": v(883.12, -363.97) * mm, "end": v(899.8, -363.97) * mm});
            skLineSegment(sketch, "E212.trimOffspring", {"start": v(903.12, -363.97) * mm, "end": v(919.8, -363.97) * mm});
            skLineSegment(sketch, "E213.trimOffspring", {"start": v(923.12, -363.97) * mm, "end": v(936.46, -363.97) * mm});
            skPoint(sketch, "E214.visualSharp", {"position": v(861.46, -363.97) * mm});
            skArc(sketch, "E214.filletArc", {"start": v(861.46, -358.97) * mm, "mid": v(862.92, -362.5) * mm, "end": v(866.46, -363.97) * mm});
            skPoint(sketch, "E215.visualSharp", {"position": v(861.46, -309.97) * mm});
            skArc(sketch, "E215.filletArc", {"start": v(866.46, -309.97) * mm, "mid": v(862.92, -311.43) * mm, "end": v(861.46, -314.97) * mm});
            skPoint(sketch, "E216.visualSharp", {"position": v(941.46, -309.97) * mm});
            skArc(sketch, "E216.filletArc", {"start": v(941.46, -314.97) * mm, "mid": v(940, -311.43) * mm, "end": v(936.46, -309.97) * mm});
            skPoint(sketch, "E217.visualSharp", {"position": v(941.46, -363.97) * mm});
            skArc(sketch, "E217.filletArc", {"start": v(936.46, -363.97) * mm, "mid": v(940, -362.5) * mm, "end": v(941.46, -358.97) * mm});
            skLineSegment(sketch, "E218", {"start": v(901.46, -313.97) * mm, "end": v(901.46, -359.97) * mm, "construction": true});
            skLineSegment(sketch, "E219.bottom", {"start": v(879.96, -323.97) * mm, "end": v(882.96, -323.97) * mm});
            skLineSegment(sketch, "E219.top", {"start": v(879.96, -327.97) * mm, "end": v(882.96, -327.97) * mm});
            skLineSegment(sketch, "E219.left", {"start": v(879.96, -323.97) * mm, "end": v(879.96, -327.97) * mm});
            skLineSegment(sketch, "E219.right", {"start": v(882.96, -323.97) * mm, "end": v(882.96, -327.97) * mm});
            skLineSegment(sketch, "E220", {"start": v(881.46, -323.97) * mm, "end": v(881.46, -327.97) * mm, "construction": true});
            skLineSegment(sketch, "E221.MirrorCS", {"start": v(879.96, -349.97) * mm, "end": v(879.96, -345.97) * mm});
            skLineSegment(sketch, "E222.MirrorCS", {"start": v(879.96, -349.97) * mm, "end": v(882.96, -349.97) * mm});
            skLineSegment(sketch, "E223.MirrorCS", {"start": v(882.96, -349.97) * mm, "end": v(882.96, -345.97) * mm});
            skLineSegment(sketch, "E224.MirrorCS", {"start": v(879.96, -345.97) * mm, "end": v(882.96, -345.97) * mm});
            skLineSegment(sketch, "E225.MirrorCS", {"start": v(921.46, -323.97) * mm, "end": v(921.46, -327.97) * mm, "construction": true});
            skLineSegment(sketch, "E226.MirrorCS", {"start": v(919.96, -323.97) * mm, "end": v(919.96, -327.97) * mm});
            skLineSegment(sketch, "E227.MirrorCS", {"start": v(922.96, -323.97) * mm, "end": v(922.96, -327.97) * mm});
            skLineSegment(sketch, "E228.MirrorCS", {"start": v(922.96, -327.97) * mm, "end": v(919.96, -327.97) * mm});
            skLineSegment(sketch, "E229.MirrorCS", {"start": v(922.96, -323.97) * mm, "end": v(919.96, -323.97) * mm});
            skLineSegment(sketch, "E230.MirrorCS", {"start": v(922.96, -345.97) * mm, "end": v(919.96, -345.97) * mm});
            skLineSegment(sketch, "E231.MirrorCS", {"start": v(922.96, -349.97) * mm, "end": v(922.96, -345.97) * mm});
            skLineSegment(sketch, "E232.MirrorCS", {"start": v(922.96, -349.97) * mm, "end": v(919.96, -349.97) * mm});
            skLineSegment(sketch, "E233.MirrorCS", {"start": v(919.96, -349.97) * mm, "end": v(919.96, -345.97) * mm});
            skLineSegment(sketch, "E234", {"start": v(42.06, -285.06) * mm, "end": v(67.06, -285.06) * mm, "construction": true});
            skLineSegment(sketch, "E235", {"start": v(67.06, -285.06) * mm, "end": v(67.06, -276.06) * mm});
            skLineSegment(sketch, "E236", {"start": v(67.06, -276.06) * mm, "end": v(70.06, -276.06) * mm});
            skLineSegment(sketch, "E237", {"start": v(70.06, -276.06) * mm, "end": v(70.06, -272.06) * mm});
            skLineSegment(sketch, "E238", {"start": v(70.06, -272.06) * mm, "end": v(67.06, -272.06) * mm});
            skLineSegment(sketch, "E239", {"start": v(67.06, -272.06) * mm, "end": v(67.06, -269.06) * mm});
            skLineSegment(sketch, "E240", {"start": v(42.06, -283.56) * mm, "end": v(50.06, -283.56) * mm});
            skLineSegment(sketch, "E241", {"start": v(50.06, -283.56) * mm, "end": v(50.06, -285.06) * mm});
            skFitSpline(sketch, "E242", {"points": [v(42.06, -283.56) * mm, v(45.1, -278.42) * mm, v(54.65, -275.56) * mm, v(63.02, -270.22) * mm, v(67.06, -269.06) * mm], "startDerivative": vector(0.28, 17.75) * mm, "endDerivative": vector(17.77, -0.5) * mm});
            skLineSegment(sketch, "E243.MirrorCS", {"start": v(70.06, -298.06) * mm, "end": v(67.06, -298.06) * mm});
            skFitSpline(sketch, "E244.MirrorCS", {"points": [v(42.06, -286.56) * mm, v(45.1, -291.7) * mm, v(54.65, -294.55) * mm, v(63.02, -299.9) * mm, v(67.06, -301.06) * mm], "startDerivative": vector(0.28, -17.75) * mm, "endDerivative": vector(17.77, 0.5) * mm});
            skLineSegment(sketch, "E245.MirrorCS", {"start": v(67.06, -294.06) * mm, "end": v(70.06, -294.06) * mm});
            skLineSegment(sketch, "E246.MirrorCS", {"start": v(70.06, -294.06) * mm, "end": v(70.06, -298.06) * mm});
            skLineSegment(sketch, "E247.MirrorCS", {"start": v(67.06, -298.06) * mm, "end": v(67.06, -301.06) * mm});
            skLineSegment(sketch, "E248.MirrorCS", {"start": v(42.06, -286.56) * mm, "end": v(50.06, -286.56) * mm});
            skLineSegment(sketch, "E249.MirrorCS", {"start": v(67.06, -285.06) * mm, "end": v(67.06, -294.06) * mm});
            skLineSegment(sketch, "E250.MirrorCS", {"start": v(50.06, -286.56) * mm, "end": v(50.06, -285.06) * mm});
            skLineSegment(sketch, "E251.MirrorCS", {"start": v(50.06, -223.37) * mm, "end": v(50.06, -224.87) * mm});
            skLineSegment(sketch, "E252.MirrorCS", {"start": v(82.06, -211.87) * mm, "end": v(82.06, -208.87) * mm});
            skLineSegment(sketch, "E253.MirrorCS", {"start": v(85.06, -211.87) * mm, "end": v(82.06, -211.87) * mm});
            skFitSpline(sketch, "E254.MirrorCS", {"points": [v(42.06, -223.37) * mm, v(45.43, -218.3) * mm, v(61.47, -216.08) * mm, v(75.42, -210.03) * mm, v(82.06, -208.87) * mm], "startDerivative": vector(0.28, 17.75) * mm, "endDerivative": vector(17.77, -0.5) * mm});
            skLineSegment(sketch, "E255.MirrorCS", {"start": v(82.06, -215.87) * mm, "end": v(85.06, -215.87) * mm});
            skLineSegment(sketch, "E256.MirrorCS", {"start": v(85.06, -215.87) * mm, "end": v(85.06, -211.87) * mm});
            skLineSegment(sketch, "E257.MirrorCS", {"start": v(42.06, -223.37) * mm, "end": v(50.06, -223.37) * mm});
            skLineSegment(sketch, "E258.MirrorCS", {"start": v(82.06, -224.87) * mm, "end": v(82.06, -215.87) * mm});
            skLineSegment(sketch, "E259.MirrorCS", {"start": v(42.06, -224.87) * mm, "end": v(82.06, -224.87) * mm, "construction": true});
            skLineSegment(sketch, "E260.MirrorCS", {"start": v(50.06, -226.37) * mm, "end": v(50.06, -224.87) * mm});
            skLineSegment(sketch, "E261.MirrorCS", {"start": v(82.06, -237.87) * mm, "end": v(82.06, -240.87) * mm});
            skLineSegment(sketch, "E262.MirrorCS", {"start": v(85.06, -237.87) * mm, "end": v(82.06, -237.87) * mm});
            skLineSegment(sketch, "E263.MirrorCS", {"start": v(82.06, -233.87) * mm, "end": v(85.06, -233.87) * mm});
            skLineSegment(sketch, "E264.MirrorCS", {"start": v(85.06, -233.87) * mm, "end": v(85.06, -237.87) * mm});
            skLineSegment(sketch, "E265.MirrorCS", {"start": v(42.06, -226.37) * mm, "end": v(50.06, -226.37) * mm});
            skLineSegment(sketch, "E266.MirrorCS", {"start": v(82.06, -224.87) * mm, "end": v(82.06, -233.87) * mm});
            skFitSpline(sketch, "E267.MirrorCS", {"points": [v(42.06, -226.37) * mm, v(45.43, -231.44) * mm, v(61.47, -233.67) * mm, v(75.42, -239.71) * mm, v(82.06, -240.87) * mm], "startDerivative": vector(0.28, -17.75) * mm, "endDerivative": vector(17.77, 0.5) * mm});
            skLineSegment(sketch, "E268.bottom", {"start": v(67.91, -25.46) * mm, "end": v(72.91, -25.46) * mm});
            skLineSegment(sketch, "E268.top", {"start": v(67.91, -50.46) * mm, "end": v(72.91, -50.46) * mm});
            skLineSegment(sketch, "E268.left", {"start": v(57.91, -35.46) * mm, "end": v(57.91, -40.46) * mm});
            skLineSegment(sketch, "E268.right", {"start": v(72.91, -25.46) * mm, "end": v(72.91, -50.46) * mm});
            skLineSegment(sketch, "E269", {"start": v(72.91, -25.46) * mm, "end": v(57.91, -50.46) * mm, "construction": true});
            skPoint(sketch, "E270.visualSharp", {"position": v(57.91, -25.46) * mm});
            skArc(sketch, "E270.filletArc", {"start": v(67.91, -25.46) * mm, "mid": v(60.84, -28.4) * mm, "end": v(57.91, -35.46) * mm});
            skPoint(sketch, "E271.visualSharp", {"position": v(57.91, -50.46) * mm});
            skArc(sketch, "E271.filletArc", {"start": v(57.91, -40.46) * mm, "mid": v(60.84, -47.54) * mm, "end": v(67.91, -50.46) * mm});
            skLineSegment(sketch, "E272", {"start": v(70.12, -114.16) * mm, "end": v(70.12, -172.29) * mm, "construction": true});
            skLineSegment(sketch, "E273", {"start": v(70.12, -172.29) * mm, "end": v(455, -172.29) * mm, "construction": true});
            skLineSegment(sketch, "E274", {"start": v(220.53, 87.48) * mm, "end": v(220.53, 62.13) * mm, "construction": true});
            skPoint(sketch, "E275", {"position": v(-157, 810) * mm});
            skLineSegment(sketch, "E276", {"start": v(65.41, -34.96) * mm, "end": v(65.41, -40.96) * mm, "construction": true});
            skCircle(sketch, "E277", {"center": v(65.41, -34.96) * mm, "radius": 1.5 * mm});
            skCircle(sketch, "E278", {"center": v(65.41, -40.96) * mm, "radius": 1.5 * mm});
            skPoint(sketch, "E279", {"position": v(65.41, -37.96) * mm});
            skPoint(sketch, "E280", {"position": v(-196.57, 162.88) * mm});
            skLineSegment(sketch, "E281.bottom", {"start": v(-196.57, 162.88) * mm, "end": v(-164.57, 162.88) * mm, "construction": true});
            skLineSegment(sketch, "E281.top", {"start": v(-196.57, 159.88) * mm, "end": v(-164.57, 159.88) * mm, "construction": true});
            skLineSegment(sketch, "E281.left", {"start": v(-196.57, 162.88) * mm, "end": v(-196.57, 159.88) * mm, "construction": true});
            skLineSegment(sketch, "E281.right", {"start": v(-164.57, 162.88) * mm, "end": v(-164.57, 159.88) * mm, "construction": true});
            skArc(sketch, "E282", {"start": v(-171.42, 187.23) * mm, "mid": v(-161.6, 161.65) * mm, "end": v(-173.2, 136.83) * mm});
            skLineSegment(sketch, "E283", {"start": v(-176.43, 182.38) * mm, "end": v(-171.42, 187.23) * mm});
            skLineSegment(sketch, "E284", {"start": v(-176.43, 139.88) * mm, "end": v(-173.2, 136.83) * mm});
            skSolve(sketch);
        }
        {
            var Q0;
            Q0 = qSketchRegion(id + "F0", true);
            extrude(context, id + "F1", {"entities" : qUnion([Q0]), "depth" : 3 * mm});
        }
        {
            var Q0;
            Q0=makeQuery(id+"F1.opExtrude","SWEPT_BODY",BODY,{"disambiguationData":[OSD([sQuery(id+"F0.wireOp",EDGE,"E11"),sQuery(id+"F0.wireOp",EDGE,"E12"),sQuery(id+"F0.wireOp",EDGE,"E13"),sQuery(id+"F0.wireOp",EDGE,"E14"),sQuery(id+"F0.wireOp",EDGE,"E15"),sQuery(id+"F0.wireOp",EDGE,"E16"),sQuery(id+"F0.wireOp",EDGE,"E17.trimOffspring"),sQuery(id+"F0.wireOp",EDGE,"E18"),sQuery(id+"F0.wireOp",EDGE,"E19"),sQuery(id+"F0.wireOp",EDGE,"E20"),sQuery(id+"F0.wireOp",EDGE,"E21"),sQuery(id+"F0.wireOp",EDGE,"E22"),sQuery(id+"F0.wireOp",EDGE,"E23"),sQuery(id+"F0.wireOp",EDGE,"E24"),sQuery(id+"F0.wireOp",EDGE,"E25"),sQuery(id+"F0.wireOp",EDGE,"E26"),sQuery(id+"F0.wireOp",EDGE,"E27"),sQuery(id+"F0.wireOp",EDGE,"E28"),sQuery(id+"F0.wireOp",EDGE,"E29"),sQuery(id+"F0.wireOp",EDGE,"E30"),sQuery(id+"F0.wireOp",EDGE,"E31"),sQuery(id+"F0.wireOp",EDGE,"E32"),sQuery(id+"F0.wireOp",EDGE,"E33"),sQuery(id+"F0.wireOp",EDGE,"E34"),sQuery(id+"F0.wireOp",EDGE,"E35"),sQuery(id+"F0.wireOp",EDGE,"E36"),sQuery(id+"F0.wireOp",EDGE,"E37"),sQuery(id+"F0.wireOp",EDGE,"E38.trimOffspring"),sQuery(id+"F0.wireOp",EDGE,"E39.trimOffspring"),sQuery(id+"F0.wireOp",EDGE,"E40.trimOffspring"),sQuery(id+"F0.wireOp",EDGE,"E41.trimOffspring"),sQuery(id+"F0.wireOp",EDGE,"E42.trimOffspring"),sQuery(id+"F0.wireOp",EDGE,"E43.trimOffspring")])]});
            var Q1;
            Q1=makeQuery(id+"F1.opExtrude","SWEPT_FACE",FACE,{"disambiguationData":[OSD([sQuery(id+"F0.wireOp",EDGE,"E41.trimOffspring")])]});
            mirror(context, id + "F2", {"operationType" : NewBodyOperationType.ADD, "entities" : qUnion([Q0]), "mirrorPlane" : qUnion([Q1])});
        }
        {
            var Q0;
            Q0=makeQuery(id+"F1.opExtrude","CAP_FACE",FACE,{"disambiguationData":[OSD([sQuery(id+"F0.wireOp",EDGE,"E64"),sQuery(id+"F0.wireOp",EDGE,"E65"),sQuery(id+"F0.wireOp",EDGE,"E66"),sQuery(id+"F0.wireOp",EDGE,"E67"),sQuery(id+"F0.wireOp",EDGE,"E68"),sQuery(id+"F0.wireOp",EDGE,"E69"),sQuery(id+"F0.wireOp",EDGE,"E70"),sQuery(id+"F0.wireOp",EDGE,"E71"),sQuery(id+"F0.wireOp",EDGE,"E72"),sQuery(id+"F0.wireOp",EDGE,"E73"),sQuery(id+"F0.wireOp",EDGE,"E74"),sQuery(id+"F0.wireOp",EDGE,"E75"),sQuery(id+"F0.wireOp",EDGE,"E76"),sQuery(id+"F0.wireOp",EDGE,"E77"),sQuery(id+"F0.wireOp",EDGE,"E78"),sQuery(id+"F0.wireOp",EDGE,"E79"),sQuery(id+"F0.wireOp",EDGE,"E80.trimOffspring"),sQuery(id+"F0.wireOp",EDGE,"E81.trimOffspring"),sQuery(id+"F0.wireOp",EDGE,"E82.trimOffspring"),sQuery(id+"F0.wireOp",EDGE,"E83.trimOffspring"),sQuery(id+"F0.wireOp",EDGE,"E84")])],"isStart":false});
            var sketch = newSketch(context, id + "F3", { "sketchPlane" : qUnion([Q0])});
            skLineSegment(sketch, "E285", {"start": v(-226.05, 1011.31) * mm, "end": v(-150.78, 1013.28) * mm});
            skLineSegment(sketch, "E286", {"start": v(-150.78, 1013.28) * mm, "end": v(-150.87, 1016.65) * mm});
            skLineSegment(sketch, "E287", {"start": v(-150.87, 1016.65) * mm, "end": v(-226.05, 1014.68) * mm});
            skLineSegment(sketch, "E288", {"start": v(-226.05, 1014.68) * mm, "end": v(-226.05, 1011.31) * mm});
            skLineSegment(sketch, "E289.bottom", {"start": v(-157, 1013.2) * mm, "end": v(-154, 1013.2) * mm, "construction": true});
            skLineSegment(sketch, "E289.top", {"start": v(-157, 1011.2) * mm, "end": v(-154, 1011.2) * mm, "construction": true});
            skLineSegment(sketch, "E289.left", {"start": v(-157, 1013.2) * mm, "end": v(-157, 1011.2) * mm, "construction": true});
            skLineSegment(sketch, "E289.right", {"start": v(-154, 1013.2) * mm, "end": v(-154, 1011.2) * mm, "construction": true});
            skSolve(sketch);
        }
        {
            var Q0;
            Q0 = qSketchRegion(id + "F3", true);
            extrude(context, id + "F4", {"entities" : qUnion([Q0]), "operationType" : NewBodyOperationType.REMOVE, "endBound" : BoundingType.THROUGH_ALL, "oppositeDirection" : true, "depth" : 25 * mm});
        }
        {
            var Q0;
            Q0=makeQuery(id+"F1.opExtrude","SWEPT_BODY",BODY,{"disambiguationData":[OSD([sQuery(id+"F0.wireOp",EDGE,"E96"),sQuery(id+"F0.wireOp",EDGE,"E97"),sQuery(id+"F0.wireOp",EDGE,"E98"),sQuery(id+"F0.wireOp",EDGE,"E99"),sQuery(id+"F0.wireOp",EDGE,"E100"),sQuery(id+"F0.wireOp",EDGE,"E101"),sQuery(id+"F0.wireOp",EDGE,"E102"),sQuery(id+"F0.wireOp",EDGE,"E103"),sQuery(id+"F0.wireOp",EDGE,"E104"),sQuery(id+"F0.wireOp",EDGE,"E105.trimOffspring"),sQuery(id+"F0.wireOp",EDGE,"E106")])]});
            var Q1;
            Q1=makeQuery(id+"F1.opExtrude","SWEPT_FACE",FACE,{"disambiguationData":[OSD([sQuery(id+"F0.wireOp",EDGE,"E96")])]});
            mirror(context, id + "F5", {"operationType" : NewBodyOperationType.ADD, "entities" : qUnion([Q0]), "mirrorPlane" : qUnion([Q1])});
        }
        {
            var Q0;
            Q0=makeQuery(id+"F1.opExtrude","SWEPT_BODY",BODY,{"disambiguationData":[OSD([sQuery(id+"F0.wireOp",EDGE,"E107"),sQuery(id+"F0.wireOp",EDGE,"E108"),sQuery(id+"F0.wireOp",EDGE,"E109"),sQuery(id+"F0.wireOp",EDGE,"E110"),sQuery(id+"F0.wireOp",EDGE,"E111"),sQuery(id+"F0.wireOp",EDGE,"E112")])]});
            var Q1;
            Q1=makeQuery(id+"F1.opExtrude","SWEPT_FACE",FACE,{"disambiguationData":[OSD([sQuery(id+"F0.wireOp",EDGE,"E109")])]});
            mirror(context, id + "F6", {"operationType" : NewBodyOperationType.ADD, "entities" : qUnion([Q0]), "mirrorPlane" : qUnion([Q1])});
        }
        {
            var Q0;
            Q0=makeQuery(id+"F1.opExtrude","SWEPT_EDGE",EDGE,{"disambiguationData":[OSD([sQuery(id+"F0.wireOp",EDGE,"E125"),sQuery(id+"F0.wireOp",EDGE,"E128")])]});
            fillet(context, id + "F7", {"entities" : qUnion([Q0]), "radius" : 2 * mm, "tangentPropagation" : true, "allowEdgeOverflow" : false});
        }
        {
            var Q0;
            Q0=makeQuery(id+"F1.opExtrude","SWEPT_EDGE",EDGE,{"disambiguationData":[OSD([sQuery(id+"F0.wireOp",EDGE,"E126"),sQuery(id+"F0.wireOp",EDGE,"E127")])]});
            fillet(context, id + "F8", {"entities" : qUnion([Q0]), "radius" : 5 * mm, "tangentPropagation" : true, "allowEdgeOverflow" : false});
        }
        {
            var Q0;
            Q0=makeQuery(id+"F1.opExtrude","SWEPT_BODY",BODY,{"disambiguationData":[OSD([sQuery(id+"F0.wireOp",EDGE,"E113"),sQuery(id+"F0.wireOp",EDGE,"E114"),sQuery(id+"F0.wireOp",EDGE,"E115"),sQuery(id+"F0.wireOp",EDGE,"E116"),sQuery(id+"F0.wireOp",EDGE,"E117"),sQuery(id+"F0.wireOp",EDGE,"E118"),sQuery(id+"F0.wireOp",EDGE,"E119"),sQuery(id+"F0.wireOp",EDGE,"E120"),sQuery(id+"F0.wireOp",EDGE,"E121"),sQuery(id+"F0.wireOp",EDGE,"E122"),sQuery(id+"F0.wireOp",EDGE,"E123"),sQuery(id+"F0.wireOp",EDGE,"E124"),sQuery(id+"F0.wireOp",EDGE,"E125"),sQuery(id+"F0.wireOp",EDGE,"E126"),sQuery(id+"F0.wireOp",EDGE,"E127"),sQuery(id+"F0.wireOp",EDGE,"E128"),sQuery(id+"F0.wireOp",EDGE,"E129"),sQuery(id+"F0.wireOp",EDGE,"E130"),sQuery(id+"F0.wireOp",EDGE,"E133.bottom"),sQuery(id+"F0.wireOp",EDGE,"E133.top"),sQuery(id+"F0.wireOp",EDGE,"E133.left"),sQuery(id+"F0.wireOp",EDGE,"E133.right"),sQuery(id+"F0.wireOp",EDGE,"E134.bottom"),sQuery(id+"F0.wireOp",EDGE,"E134.top"),sQuery(id+"F0.wireOp",EDGE,"E134.left"),sQuery(id+"F0.wireOp",EDGE,"E134.right")])]});
            var Q1;
            Q1=makeQuery(id+"F1.opExtrude","SWEPT_FACE",FACE,{"disambiguationData":[OSD([sQuery(id+"F0.wireOp",EDGE,"E115")])]});
            mirror(context, id + "F9", {"entities" : qUnion([Q0]), "mirrorPlane" : qUnion([Q1])});
        }
        {
            var Q0;
            Q0=makeQuery(id+"F1.opExtrude","CAP_FACE",FACE,{"disambiguationData":[OSD([sQuery(id+"F0.wireOp",EDGE,"E113"),sQuery(id+"F0.wireOp",EDGE,"E114"),sQuery(id+"F0.wireOp",EDGE,"E115"),sQuery(id+"F0.wireOp",EDGE,"E116"),sQuery(id+"F0.wireOp",EDGE,"E117"),sQuery(id+"F0.wireOp",EDGE,"E118"),sQuery(id+"F0.wireOp",EDGE,"E119"),sQuery(id+"F0.wireOp",EDGE,"E120"),sQuery(id+"F0.wireOp",EDGE,"E121"),sQuery(id+"F0.wireOp",EDGE,"E122"),sQuery(id+"F0.wireOp",EDGE,"E123"),sQuery(id+"F0.wireOp",EDGE,"E124"),sQuery(id+"F0.wireOp",EDGE,"E125"),sQuery(id+"F0.wireOp",EDGE,"E126"),sQuery(id+"F0.wireOp",EDGE,"E127"),sQuery(id+"F0.wireOp",EDGE,"E128"),sQuery(id+"F0.wireOp",EDGE,"E129"),sQuery(id+"F0.wireOp",EDGE,"E130"),sQuery(id+"F0.wireOp",EDGE,"E133.bottom"),sQuery(id+"F0.wireOp",EDGE,"E133.top"),sQuery(id+"F0.wireOp",EDGE,"E133.left"),sQuery(id+"F0.wireOp",EDGE,"E133.right"),sQuery(id+"F0.wireOp",EDGE,"E134.bottom"),sQuery(id+"F0.wireOp",EDGE,"E134.top"),sQuery(id+"F0.wireOp",EDGE,"E134.left"),sQuery(id+"F0.wireOp",EDGE,"E134.right")])],"isStart":false});
            var sketch = newSketch(context, id + "F10", { "sketchPlane" : qUnion([Q0])});
            skLineSegment(sketch, "E290.bottom", {"start": v(157.1, 351.54) * mm, "end": v(175.1, 351.54) * mm});
            skLineSegment(sketch, "E290.top", {"start": v(157.1, 345.54) * mm, "end": v(175.1, 345.54) * mm});
            skLineSegment(sketch, "E291.bottom", {"start": v(211.1, 351.54) * mm, "end": v(225.1, 351.54) * mm});
            skLineSegment(sketch, "E291.top", {"start": v(211.1, 345.54) * mm, "end": v(225.1, 345.54) * mm});
            skArc(sketch, "E292", {"start": v(157.1, 351.54) * mm, "mid": v(154.1, 348.54) * mm, "end": v(157.1, 345.54) * mm});
            skArc(sketch, "E293", {"start": v(175.1, 351.54) * mm, "mid": v(178.1, 348.54) * mm, "end": v(175.1, 345.54) * mm});
            skArc(sketch, "E294", {"start": v(211.1, 351.54) * mm, "mid": v(208.1, 348.54) * mm, "end": v(211.1, 345.54) * mm});
            skArc(sketch, "E295", {"start": v(225.1, 351.54) * mm, "mid": v(228.1, 348.54) * mm, "end": v(225.1, 345.54) * mm});
            skSolve(sketch);
        }
        {
            var Q0;
            Q0 = qSketchRegion(id + "F10", true);
            extrude(context, id + "F11", {"entities" : qUnion([Q0]), "operationType" : NewBodyOperationType.REMOVE, "endBound" : BoundingType.THROUGH_ALL, "oppositeDirection" : true, "depth" : 25 * mm});
        }
        {
            var Q0;
            Q0=qCreatedBy(makeId("Top.planeOp"),FACE);
            var Q1;
            Q1=makeQuery(id+"F1.opExtrude","CAP_VERTEX",VERTEX,{"disambiguationData":[OSD([sQuery(id+"F0.wireOp",EDGE,"E161"),sQuery(id+"F0.wireOp",EDGE,"E165")])],"isStart":false});
            cPlane(context, id + "F12", {"entities" : qUnion([Q0, Q1]), "cplaneType" : CPlaneType.PLANE_POINT, "offset" : 0 * mm, "width" : 150 * mm, "height" : 150 * mm});
        }
        {
            var Q0;
            Q0=qCreatedBy(id+"F12.planeOp",FACE);
            var sketch = newSketch(context, id + "F13", { "sketchPlane" : qUnion([Q0])});
            skPoint(sketch, "E296.0", {"position": v(3, 729.86) * mm});
            skLineSegment(sketch, "E297", {"start": v(3, 729.86) * mm, "end": v(-54.32, 782.76) * mm});
            skLineSegment(sketch, "E298", {"start": v(-54.32, 782.76) * mm, "end": v(-54.32, 729.86) * mm});
            skLineSegment(sketch, "E299", {"start": v(-54.32, 729.86) * mm, "end": v(3, 729.86) * mm});
            skLineSegment(sketch, "E300", {"start": v(3, 729.86) * mm, "end": v(3, 844.86) * mm, "construction": true});
            skLineSegment(sketch, "E301", {"start": v(3, 844.86) * mm, "end": v(-54.32, 782.76) * mm});
            skLineSegment(sketch, "E302", {"start": v(3, 844.86) * mm, "end": v(-54.32, 844.86) * mm});
            skLineSegment(sketch, "E303", {"start": v(-54.32, 844.86) * mm, "end": v(-54.32, 782.76) * mm});
            skSolve(sketch);
        }
        {
            var Q0;
            Q0 = qSketchRegion(id + "F13", true);
            extrude(context, id + "F14", {"entities" : qUnion([Q0]), "operationType" : NewBodyOperationType.REMOVE, "endBound" : BoundingType.THROUGH_ALL, "depth" : 25 * mm});
        }
        {
            var Q0;
            Q0=makeQuery(id+"F1.opExtrude","SWEPT_BODY",BODY,{"disambiguationData":[OSD([sQuery(id+"F0.wireOp",EDGE,"E161"),sQuery(id+"F0.wireOp",EDGE,"E162"),sQuery(id+"F0.wireOp",EDGE,"E163"),sQuery(id+"F0.wireOp",EDGE,"E164"),sQuery(id+"F0.wireOp",EDGE,"E165"),sQuery(id+"F0.wireOp",EDGE,"E166"),sQuery(id+"F0.wireOp",EDGE,"E167"),sQuery(id+"F0.wireOp",EDGE,"E168"),sQuery(id+"F0.wireOp",EDGE,"E169"),sQuery(id+"F0.wireOp",EDGE,"E170")])]});
            var Q1;
            Q1=qCreatedBy(id+"F12.planeOp",FACE);
            mirror(context, id + "F15", {"entities" : qUnion([Q0]), "mirrorPlane" : qUnion([Q1])});
        }
        {
            var Q0;
            Q0=makeQuery(id+"F1.opExtrude","CAP_FACE",FACE,{"disambiguationData":[OSD([sQuery(id+"F0.wireOp",EDGE,"E64"),sQuery(id+"F0.wireOp",EDGE,"E65"),sQuery(id+"F0.wireOp",EDGE,"E66"),sQuery(id+"F0.wireOp",EDGE,"E67"),sQuery(id+"F0.wireOp",EDGE,"E68"),sQuery(id+"F0.wireOp",EDGE,"E69"),sQuery(id+"F0.wireOp",EDGE,"E70"),sQuery(id+"F0.wireOp",EDGE,"E71"),sQuery(id+"F0.wireOp",EDGE,"E72"),sQuery(id+"F0.wireOp",EDGE,"E73"),sQuery(id+"F0.wireOp",EDGE,"E74"),sQuery(id+"F0.wireOp",EDGE,"E75"),sQuery(id+"F0.wireOp",EDGE,"E76"),sQuery(id+"F0.wireOp",EDGE,"E77"),sQuery(id+"F0.wireOp",EDGE,"E78"),sQuery(id+"F0.wireOp",EDGE,"E79"),sQuery(id+"F0.wireOp",EDGE,"E80.trimOffspring"),sQuery(id+"F0.wireOp",EDGE,"E81.trimOffspring"),sQuery(id+"F0.wireOp",EDGE,"E82.trimOffspring"),sQuery(id+"F0.wireOp",EDGE,"E83.trimOffspring"),sQuery(id+"F0.wireOp",EDGE,"E84"),sQuery(id+"F0.wireOp",EDGE,"E131.bottom"),sQuery(id+"F0.wireOp",EDGE,"E131.top"),sQuery(id+"F0.wireOp",EDGE,"E131.left"),sQuery(id+"F0.wireOp",EDGE,"E131.right"),sQuery(id+"F0.wireOp",EDGE,"E132.bottom"),sQuery(id+"F0.wireOp",EDGE,"E132.top"),sQuery(id+"F0.wireOp",EDGE,"E132.left"),sQuery(id+"F0.wireOp",EDGE,"E132.right")])],"isStart":false});
            var sketch = newSketch(context, id + "F16", { "sketchPlane" : qUnion([Q0])});
            skLineSegment(sketch, "E304.bottom", {"start": v(-180.22, 311.32) * mm, "end": v(-156.18, 336.76) * mm, "construction": true});
            skLineSegment(sketch, "E304.top", {"start": v(-178.04, 309.26) * mm, "end": v(-154, 334.7) * mm, "construction": true});
            skLineSegment(sketch, "E304.left", {"start": v(-180.22, 311.32) * mm, "end": v(-178.04, 309.26) * mm, "construction": true});
            skLineSegment(sketch, "E304.right", {"start": v(-156.18, 336.76) * mm, "end": v(-154, 334.7) * mm, "construction": true});
            skLineSegment(sketch, "E305", {"start": v(-177, 314.56) * mm, "end": v(-157.97, 334.7) * mm});
            skLineSegment(sketch, "E306", {"start": v(-157.97, 334.7) * mm, "end": v(-153.17, 334.7) * mm});
            skLineSegment(sketch, "E307", {"start": v(-153.17, 334.7) * mm, "end": v(-153.17, 314.56) * mm});
            skLineSegment(sketch, "E308", {"start": v(-153.17, 314.56) * mm, "end": v(-177, 314.56) * mm});
            skSolve(sketch);
        }
        {
            var Q0;
            Q0 = qSketchRegion(id + "F16", true);
            extrude(context, id + "F17", {"entities" : qUnion([Q0]), "operationType" : NewBodyOperationType.REMOVE, "endBound" : BoundingType.THROUGH_ALL, "oppositeDirection" : true, "depth" : 25 * mm});
        }
        {
            var Q0;
            Q0=qCreatedBy(makeId("Front.planeOp"),FACE);
            var Q1;
            Q1=sQuery(id+"F0.wireOp",VERTEX,"E109.start");
            cPlane(context, id + "F18", {"entities" : qUnion([Q0, Q1]), "cplaneType" : CPlaneType.PLANE_POINT, "offset" : 0 * mm, "width" : 150 * mm, "height" : 150 * mm});
        }
        {
            var Q0;
            Q0=qCreatedBy(id+"F18.planeOp",FACE);
            var sketch = newSketch(context, id + "F19", { "sketchPlane" : qUnion([Q0])});
            skLineSegment(sketch, "E309.0.1", {"start": v(0, 87.48) * mm, "end": v(3, 87.48) * mm});
            skLineSegment(sketch, "E309.0.3", {"start": v(3, 87.48) * mm, "end": v(0, 87.48) * mm});
            skLineSegment(sketch, "E310", {"start": v(0, 87.48) * mm, "end": v(0, 84.03) * mm});
            skLineSegment(sketch, "E311", {"start": v(0, 84.03) * mm, "end": v(3, 87.48) * mm});
            skSolve(sketch);
        }
        {
            var Q0;
            Q0 = qSketchRegion(id + "F19", true);
            extrude(context, id + "F20", {"entities" : qUnion([Q0]), "operationType" : NewBodyOperationType.REMOVE, "depth" : 319 * mm, "symmetric" : true});
        }
        {
            var Q0;
            Q0=sQuery(id+"F0.wireOp",VERTEX,"E175.end");
            var Q1;
            Q1=qCreatedBy(makeId("Front.planeOp"),FACE);
            cPlane(context, id + "F21", {"entities" : qUnion([Q0, Q1]), "cplaneType" : CPlaneType.PLANE_POINT, "offset" : 25 * mm, "width" : 150 * mm, "height" : 150 * mm});
        }
        {
            var Q0;
            Q0=qCreatedBy(id+"F21.planeOp",FACE);
            var sketch = newSketch(context, id + "F22", { "sketchPlane" : qUnion([Q0])});
            skPoint(sketch, "E312.0", {"position": v(3, -21.62) * mm});
            skPoint(sketch, "E313.0", {"position": v(3, -296.62) * mm});
            skLineSegment(sketch, "E314", {"start": v(3, -296.62) * mm, "end": v(3, -21.62) * mm, "construction": true});
            skLineSegment(sketch, "E315", {"start": v(3, -21.62) * mm, "end": v(-83.05, -21.62) * mm});
            skLineSegment(sketch, "E316", {"start": v(-83.05, -21.62) * mm, "end": v(-83.05, -296.62) * mm});
            skLineSegment(sketch, "E317", {"start": v(-83.05, -296.62) * mm, "end": v(3, -296.62) * mm});
            skLineSegment(sketch, "E318", {"start": v(3, -296.62) * mm, "end": v(-83.05, -51.87) * mm});
            skLineSegment(sketch, "E319", {"start": v(-83.05, -51.87) * mm, "end": v(3, -21.62) * mm});
            skSolve(sketch);
        }
        {
            var Q0;
            Q0 = qSketchRegion(id + "F22", true);
            var Q1;
            Q1=sQuery(id+"F0.wireOp",VERTEX,"E173.end");
            extrude(context, id + "F23", {"entities" : qUnion([Q0]), "operationType" : NewBodyOperationType.REMOVE, "endBound" : BoundingType.UP_TO_VERTEX, "oppositeDirection" : true, "endBoundEntityVertex" : qUnion([Q1]), "depth" : 25 * mm});
        }
        {
            var Q0;
            Q0=qCreatedBy(makeId("Front.planeOp"),FACE);
            var Q1;
            Q1=sQuery(id+"F0.wireOp",VERTEX,"E173.end");
            cPlane(context, id + "F24", {"entities" : qUnion([Q0, Q1]), "cplaneType" : CPlaneType.PLANE_POINT, "offset" : 25 * mm, "width" : 150 * mm, "height" : 150 * mm});
        }
        {
            var Q0;
            Q0=makeQuery(id+"F1.opExtrude","SWEPT_BODY",BODY,{"disambiguationData":[OSD([sQuery(id+"F0.wireOp",EDGE,"E171"),sQuery(id+"F0.wireOp",EDGE,"E172"),sQuery(id+"F0.wireOp",EDGE,"E173"),sQuery(id+"F0.wireOp",EDGE,"E174"),sQuery(id+"F0.wireOp",EDGE,"E175"),sQuery(id+"F0.wireOp",EDGE,"E176"),sQuery(id+"F0.wireOp",EDGE,"E177"),sQuery(id+"F0.wireOp",EDGE,"E178")])]});
            var Q1;
            Q1=qCreatedBy(id+"F24.planeOp",FACE);
            mirror(context, id + "F25", {"entities" : qUnion([Q0]), "mirrorPlane" : qUnion([Q1])});
        }
        {
            var Q0;
            Q0=makeQuery(id+"F20.boolean.opBoolean","COPY",VERTEX,{"derivedFrom":makeQuery(id+"F20.opExtrude","CAP_VERTEX",VERTEX,{"disambiguationData":[OSD([sQuery(id+"F19.wireOp",EDGE,"E310"),sQuery(id+"F19.wireOp",EDGE,"E311")])],"isStart":false})});
            var Q1;
            Q1=sQuery(id+"F0.wireOp",VERTEX,"E107.start");
            var Q2;
            Q2=makeQuery(id+"F20.boolean.opBoolean","MERGE",VERTEX,{"derivedFrom":[makeQuery(id+"F1.opExtrude","CAP_VERTEX",VERTEX,{"disambiguationData":[OSD([sQuery(id+"F0.wireOp",EDGE,"E107"),sQuery(id+"F0.wireOp",EDGE,"E108")])],"isStart":false}),makeQuery(id+"F20.opExtrude","CAP_VERTEX",VERTEX,{"disambiguationData":[OSD([sQuery(id+"F19.wireOp",EDGE,"E309.0.3"),sQuery(id+"F19.wireOp",EDGE,"E311")])],"isStart":false})]});
            cPlane(context, id + "F26", {"entities" : qUnion([Q0, Q1, Q2]), "cplaneType" : CPlaneType.THREE_POINT, "offset" : 25 * mm, "width" : 150 * mm, "height" : 150 * mm});
        }
        {
            var Q0;
            Q0=qCreatedBy(id+"F26.planeOp",FACE);
            var sketch = newSketch(context, id + "F27", { "sketchPlane" : qUnion([Q0])});
            skLineSegment(sketch, "E320.0", {"start": v(55.47, 33.14) * mm, "end": v(58.88, 36.2) * mm});
            skLineSegment(sketch, "E321", {"start": v(58.88, 36.2) * mm, "end": v(60.86, 79.83) * mm});
            skLineSegment(sketch, "E322", {"start": v(60.86, 79.83) * mm, "end": v(44.48, 81.95) * mm});
            skLineSegment(sketch, "E323", {"start": v(44.48, 81.95) * mm, "end": v(55.47, 33.14) * mm});
            skSolve(sketch);
        }
        {
            var Q0;
            Q0 = qSketchRegion(id + "F27", true);
            extrude(context, id + "F28", {"entities" : qUnion([Q0]), "operationType" : NewBodyOperationType.REMOVE, "oppositeDirection" : true, "depth" : 2 * mm});
        }
        {
            var Q0;
            Q0=makeQuery(id+"F20.boolean.opBoolean","COPY",VERTEX,{"derivedFrom":makeQuery(id+"F20.opExtrude","CAP_VERTEX",VERTEX,{"disambiguationData":[OSD([sQuery(id+"F19.wireOp",EDGE,"E310"),sQuery(id+"F19.wireOp",EDGE,"E311")])],"isStart":true})});
            var Q1;
            Q1=makeQuery(id+"F20.boolean.opBoolean","MERGE",VERTEX,{"derivedFrom":[makeQuery(id+"F6.opPattern","COPY",VERTEX,{"derivedFrom":makeQuery(id+"F1.opExtrude","CAP_VERTEX",VERTEX,{"disambiguationData":[OSD([sQuery(id+"F0.wireOp",EDGE,"E107"),sQuery(id+"F0.wireOp",EDGE,"E108")])],"isStart":false}),"instanceName":"1"}),makeQuery(id+"F20.opExtrude","CAP_VERTEX",VERTEX,{"disambiguationData":[OSD([sQuery(id+"F19.wireOp",EDGE,"E309.0.3"),sQuery(id+"F19.wireOp",EDGE,"E311")])],"isStart":true})]});
            var Q2;
            Q2=makeQuery(id+"F6.opPattern","COPY",VERTEX,{"derivedFrom":makeQuery(id+"F1.opExtrude","CAP_VERTEX",VERTEX,{"disambiguationData":[OSD([sQuery(id+"F0.wireOp",EDGE,"E107"),sQuery(id+"F0.wireOp",EDGE,"E112")])],"isStart":true}),"instanceName":"1"});
            cPlane(context, id + "F29", {"entities" : qUnion([Q0, Q1, Q2]), "cplaneType" : CPlaneType.THREE_POINT, "offset" : 25 * mm, "width" : 150 * mm, "height" : 150 * mm});
        }
        {
            var Q0;
            Q0=qCreatedBy(id+"F29.planeOp",FACE);
            var sketch = newSketch(context, id + "F30", { "sketchPlane" : qUnion([Q0])});
            skLineSegment(sketch, "E324.0", {"start": v(151.82, 264.14) * mm, "end": v(148.42, 267.2) * mm});
            skLineSegment(sketch, "E325", {"start": v(148.42, 267.2) * mm, "end": v(142.47, 312.38) * mm});
            skLineSegment(sketch, "E326", {"start": v(142.47, 312.38) * mm, "end": v(164.1, 313.8) * mm});
            skLineSegment(sketch, "E327", {"start": v(164.1, 313.8) * mm, "end": v(151.82, 264.14) * mm});
            skSolve(sketch);
        }
        {
            var Q0;
            Q0 = qSketchRegion(id + "F30", true);
            extrude(context, id + "F31", {"entities" : qUnion([Q0]), "operationType" : NewBodyOperationType.REMOVE, "oppositeDirection" : true, "depth" : 2 * mm});
        }
        {
            var Q0;
            Q0=makeQuery(id+"F1.opExtrude","SWEPT_FACE",FACE,{"disambiguationData":[OSD([sQuery(id+"F0.wireOp",EDGE,"E179.left")])]});
            var Q1;
            Q1=sQuery(id+"F0.wireOp",VERTEX,"E179.left.start");
            cPlane(context, id + "F32", {"entities" : qUnion([Q0, Q1]), "cplaneType" : CPlaneType.PLANE_POINT, "offset" : 25 * mm, "width" : 150 * mm, "height" : 150 * mm});
        }
        {
            var Q0;
            Q0=qCreatedBy(id+"F32.planeOp",FACE);
            var sketch = newSketch(context, id + "F33", { "sketchPlane" : qUnion([Q0])});
            skLineSegment(sketch, "E328.0.0", {"start": v(0, -317.88) * mm, "end": v(0, -320.88) * mm});
            skLineSegment(sketch, "E328.0.1", {"start": v(0, -349.88) * mm, "end": v(3, -349.88) * mm});
            skLineSegment(sketch, "E328.0.3", {"start": v(3, -317.88) * mm, "end": v(0, -317.88) * mm});
            skLineSegment(sketch, "E329", {"start": v(3, -317.88) * mm, "end": v(0, -320.88) * mm});
            skLineSegment(sketch, "E330", {"start": v(3, -349.88) * mm, "end": v(0, -346.88) * mm});
            skLineSegment(sketch, "E331.trimOffspring", {"start": v(0, -346.88) * mm, "end": v(0, -349.88) * mm});
            skSolve(sketch);
        }
        {
            var Q0;
            Q0 = qSketchRegion(id + "F33", true);
            extrude(context, id + "F34", {"entities" : qUnion([Q0]), "operationType" : NewBodyOperationType.REMOVE, "endBound" : BoundingType.UP_TO_NEXT, "oppositeDirection" : true, "depth" : 25 * mm});
        }
    });
